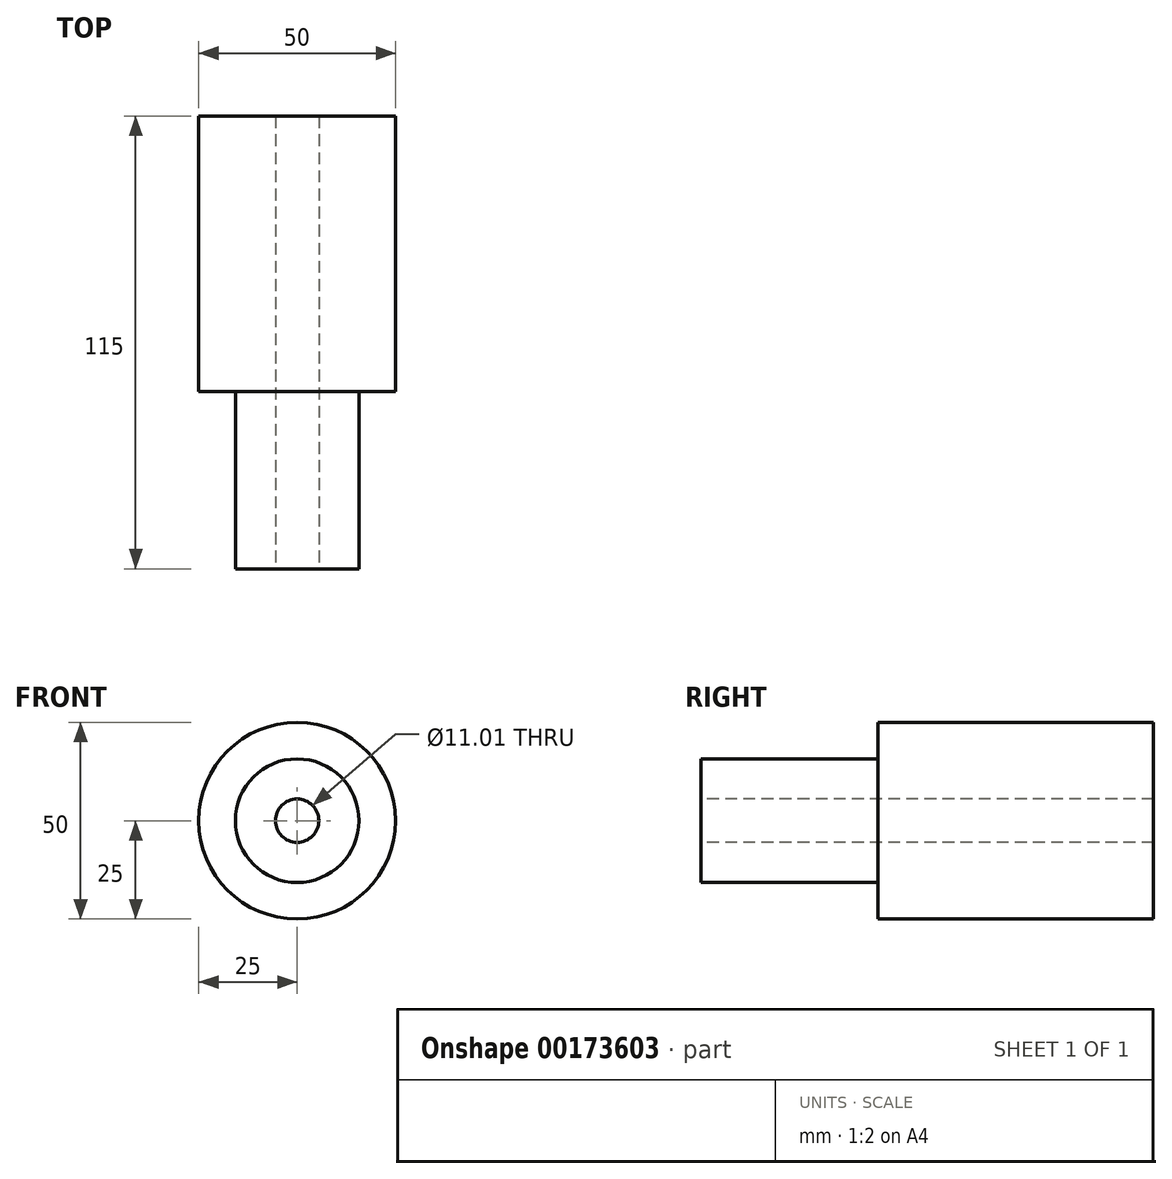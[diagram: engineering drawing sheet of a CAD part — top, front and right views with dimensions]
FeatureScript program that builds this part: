
annotation { "Feature Type Name" : "Feature", "Feature Type Description" : "" }
export const myFeature = defineFeature(function(context is Context, id is Id, definition is map)
    precondition{}
    {
        {
            var Q0;
            Q0=qCreatedBy(makeId("Front.planeOp"),FACE);
            var sketch = newSketch(context, id + "F0", { "sketchPlane" : qUnion([Q0])});
            skCircle(sketch, "E0", {"center": v(0, 0) * mm, "radius": 25 * mm});
            skSolve(sketch);
        }
        {
            var Q0;
            Q0=makeQuery(id+"F0.imprint","IMPRINT",FACE,{"disambiguationData":[TD([[makeQuery(id+"F0.imprint","IMPRINT",EDGE,{"derivedFrom":sQuery(id+"F0.wireOp",EDGE,"E0")}),1.0]])]});
            extrude(context, id + "F1", {"entities" : qUnion([Q0]), "depth" : 70 * mm});
        }
        {
            var Q0;
            Q0=makeQuery(id+"F1.opExtrude","CAP_FACE",FACE,{"disambiguationData":[OSD([sQuery(id+"F0.wireOp",EDGE,"E0")])],"isStart":false});
            var sketch = newSketch(context, id + "F2", { "sketchPlane" : qUnion([Q0])});
            skCircle(sketch, "E1", {"center": v(0, 0) * mm, "radius": 15.7 * mm});
            skSolve(sketch);
        }
        {
            var Q0;
            Q0=makeQuery(id+"F2.imprint","IMPRINT",FACE,{"disambiguationData":[TD([[makeQuery(id+"F2.imprint","IMPRINT",EDGE,{"derivedFrom":sQuery(id+"F2.wireOp",EDGE,"E1")}),1.0]])]});
            var Q1;
            Q1=sQuery(id+"F2.wireOp",EDGE,"E1");
            extrude(context, id + "F3", {"entities" : qUnion([Q0]), "operationType" : NewBodyOperationType.ADD, "surfaceEntities" : qUnion([Q1]), "depth" : 45 * mm});
        }
        {
            var Q0;
            Q0=makeQuery(id+"F3.opExtrude","CAP_FACE",FACE,{"disambiguationData":[OSD([sQuery(id+"F2.wireOp",EDGE,"E1")])],"isStart":false});
            var sketch = newSketch(context, id + "F4", { "sketchPlane" : qUnion([Q0])});
            skCircle(sketch, "E2", {"center": v(0, 0) * mm, "radius": 5.5 * mm});
            skLineSegment(sketch, "E3", {"start": v(-54.85, 51.77) * mm, "end": v(-54.85, 0) * mm});
            skLineSegment(sketch, "E4", {"start": v(-54.85, 0) * mm, "end": v(-39.3, 0) * mm});
            skLineSegment(sketch, "E5", {"start": v(-39.3, 0) * mm, "end": v(-54.85, 51.77) * mm});
            skSolve(sketch);
        }
        {
            var Q0;
            Q0 = qSketchRegion(id + "F4", true);
            var Q1;
            Q1=sQuery(id+"F4.wireOp",EDGE,"E2");
            extrude(context, id + "F5", {"entities" : qUnion([Q0]), "operationType" : NewBodyOperationType.REMOVE, "surfaceEntities" : qUnion([Q1]), "endBound" : BoundingType.THROUGH_ALL, "oppositeDirection" : true, "depth" : 10 * mm});
        }
    });
